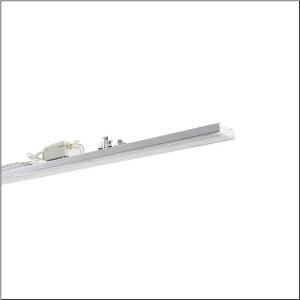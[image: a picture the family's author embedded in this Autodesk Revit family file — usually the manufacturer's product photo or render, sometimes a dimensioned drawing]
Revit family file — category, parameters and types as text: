
# Revit family: licross_11_recessed_mo_51tl11dv4fxg
name_source: partatom
category: Lighting Fixtures
units: mm (PartAtom-declared; Revit-internal decimal feet)

## family parameters
Cut with Voids When Loaded = No
Host = Face
Light Source = No
Part Type = Normal
Room Calculation Point = No
Round Connector Dimension = Use Diameter
Shared = No

## types (1)
- --- (1 x LED, 15120 lm, 84.1 W, 4000K)
    Apparent Load = 84 VA
    CIE Flux Codes = 89 96 99 100 100
    Color Rendering = 80
    Color Temperature = 4000K
    Default Elevation = 1800 mm
    Description = Licross 11 Recessed MO, luminaire insert, of sheet steel, coil coated, white, length: 2.250mm, width: 66mm, height: 67mm, LED rated luminous flux: 15.120lm, light colour: 840, SDCM (Standard Deviation of Colour Matching)MacAdam ≤ 2 SDCM (initial), control gear: DALI 2, with plug, 5-pole, with phase selection, mains connection: 220..240V, AC, 50/60Hz, rated input power: 84W, internal wiring halogen-free, primary light control with lens, of plastic, primary optical cover: cover, of PMMA, light emission: direct distribution, primary light characteristic: symmetric, protection rating (complete): IP40, insulation class (complete): insulation class I (protective earthing), certification: CE, ENEC, VDE, UKCA, protection symbol: D if used in an environment without relevant dust loads with corresponding accessories, impact resistance: IK06, permissible ambient temperature for indoor applications: -25..+35°C, corresponds to IFS (International Featured Standards) requirements for safety and quality in the food industry, reducing of maximum allowable ambient temperature of 5°C with ceiling mounting, LABS conformity tested according to VDMA 24364:2018-05, The light source and the operating device comply with the requirements of the Ecodesign Regulation (EU) 2019/2020 and are replaceable in accordance with this regulation, packaging unit: 1 piece
    Height = 58 mm
    Lamp = 1 x LED
    Lamp Light Flux = 15120 lm
    Lamp Power = 84.1 W
    Lamp count = 1
    Length = 2250 mm
    Luminous efficacy = 180 lm/W
    Manufacturer = Siteco
    ModVariant = No
    Model = 51TL11DV4FXG
    Mounting Place = Ceiling
    Mounting Type = Pendant
    Number of Poles = 1
    OnlyDefault = Yes
    Power Factor = 1
    Product Name = Licross 11 Recessed MO
    Product group = luminaire insert | ceiling pendant
    ProductGroupID = 901
    Protection Class = Protection class I
    Protection Degree = IP 40
    RLX_Detail_Level = 1
    RLX_Emergency_Light_Flux = 0 lm
    RLX_Emergency_Type = 0
    RLX_Emergency_Type_DB = No
    RlxData = <blob elided: 29873 chars, md5=73af9672>
    Socket = socket
    Standby Power = 0 W
    System Light Flux = 15120 lm
    System Power = 84 W
    Type Comments = factory setting: luminous flux: 100 % | dim-lin: 254 | 378 mA
    Type Image = l_1296930.jpg
    URL = http://relux.com
    VarID = @adj_101751
    Voltage = 0 V
    Weight = 0.00 kg
    Width = 66 mm

## geometry (parser evidence)
native form markers: Blend x4, Sweep x12
no freeform markers — native parametric forms only
